# Revit family: SNS Mini Merlin CH4CO TFT Monitor
name_source: partatom
category: Electrical Equipment
units: mm (PartAtom-declared; Revit-internal decimal feet)

## family parameters
Always vertical = Yes
Cut with Voids When Loaded = No
OmniClass Number = 23.80.30.11.17
OmniClass Title = Distribution Boards and Control Panels
Part Type = Other Panel
Room Calculation Point = No
Round Connector Dimension = Use Diameter
Shared = No
Work Plane-Based = No

## types (1)
- SNS Mini Merlin
    Default Height = 4' - 0"
    Description = The Mini Merlin is a dual gas sensor carefully designed and tested to monitor Natural Gas – Methane (CH4) and Carbon Monoxide (CO) in the air. If there is a dangerous build-up of gas or unsafe levels of carbon monoxide at the sensor, this device can shut off the gas supply via a gas safety valve and/or a gas fire appliance.
    Load = 120 VA
    Manufacturer = S&S Northern Ltd.
    Model = SNS Mini Merlin CH4CO TFT
    Product Information = https://snsnorthern.com
    Type Comments = The Mini Merlin is a dual gas sensor carefully designed and tested to monitor Natural Gas – Methane (CH4) and Carbon Monoxide (CO) in the air. If there is a dangerous build-up of gas or unsafe levels of carbon monoxide at the sensor, this device can shut off the gas supply via a gas safety valve and/or a gas fire appliance.
    URL = https://snsnorthern.com
    Voltage = 120VAC

## geometry (parser evidence)
native form markers: Sweep x27
no freeform markers — native parametric forms only
